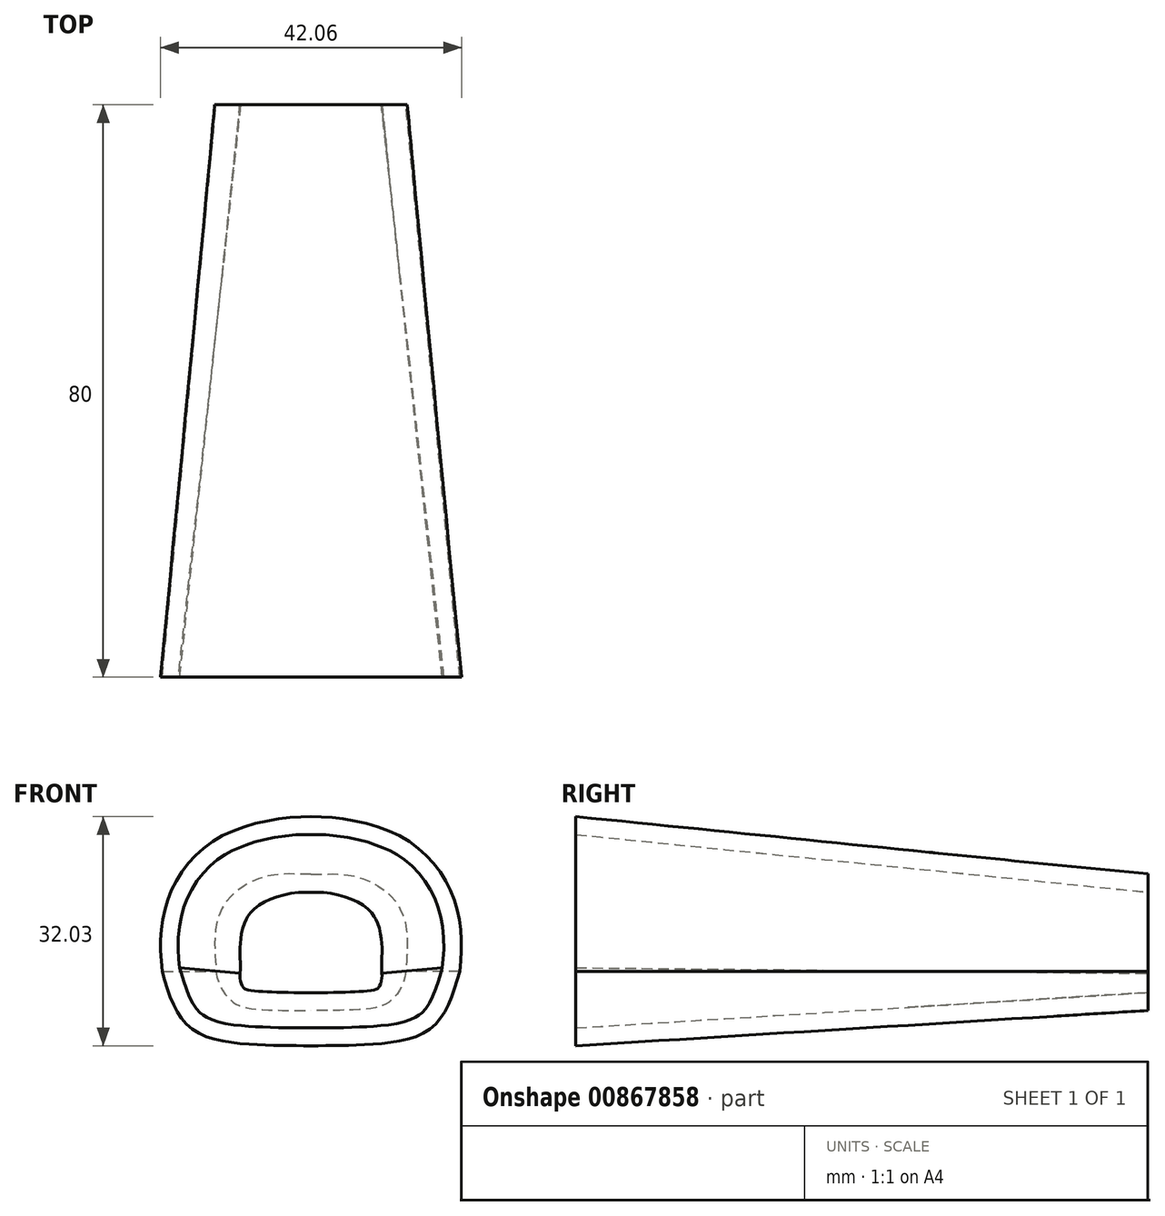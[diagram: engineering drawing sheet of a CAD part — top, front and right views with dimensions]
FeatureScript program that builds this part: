
annotation { "Feature Type Name" : "Feature", "Feature Type Description" : "" }
export const myFeature = defineFeature(function(context is Context, id is Id, definition is map)
    precondition{}
    {
        {
            var Q0;
            Q0=qCreatedBy(makeId("Front.planeOp"),FACE);
            var sketch = newSketch(context, id + "F0", { "sketchPlane" : qUnion([Q0])});
            skCircle(sketch, "E0", {"center": v(0, 50) * mm, "radius": 17.5 * mm, "construction": true});
            skSolve(sketch);
        }
        {
            var Q0;
            Q0=qCreatedBy(makeId("Front.planeOp"),FACE);
            var sketch = newSketch(context, id + "F1", { "sketchPlane" : qUnion([Q0])});
            skPoint(sketch, "E1", {"position": v(0, 50) * mm});
            skFitSpline(sketch, "E2", {"points": [v(-20.8, 50) * mm, v(-19.86, 60.47) * mm, v(-12.52, 68.9) * mm, v(0, 71.66) * mm], "startDerivative": vector(-4.23, 34.04) * mm, "endDerivative": vector(31.33, 0) * mm});
            skLineSegment(sketch, "E3", {"start": v(0, 95) * mm, "end": v(0, 106.5) * mm, "construction": true});
            skFitSpline(sketch, "E4.MirrorCS", {"points": [v(20.8, 50) * mm, v(19.86, 60.47) * mm, v(12.52, 68.9) * mm, v(0, 71.66) * mm], "startDerivative": vector(4.23, 34.04) * mm, "endDerivative": vector(-31.33, 0) * mm});
            skLineSegment(sketch, "E5", {"start": v(-101.18, 50) * mm, "end": v(-77.57, 50) * mm, "construction": true});
            skFitSpline(sketch, "E6", {"points": [v(-20.8, 50) * mm, v(-16.8, 42.08) * mm, v(-7.87, 39.8) * mm, v(0, 39.63) * mm], "startDerivative": vector(8, -27.5) * mm, "endDerivative": vector(23.5, -0.08) * mm});
            skFitSpline(sketch, "E7.MirrorCS", {"points": [v(20.8, 50) * mm, v(16.8, 42.08) * mm, v(7.87, 39.8) * mm, v(0, 39.63) * mm], "startDerivative": vector(-8, -27.5) * mm, "endDerivative": vector(-23.5, -0.08) * mm});
            skFitSpline(sketch, "E8.0", {"points": [v(-18.31, 50.3) * mm, v(-18.48, 51.63) * mm, v(-18.6, 53.56) * mm, v(-18.42, 56) * mm, v(-18.12, 57.75) * mm, v(-17.62, 59.42) * mm, v(-16.9, 61.04) * mm, v(-15.98, 62.58) * mm, v(-14.85, 64) * mm, v(-13.51, 65.28) * mm, v(-12.23, 66.2) * mm, v(-11.11, 66.83) * mm, v(-10.2, 67.26) * mm, v(-9.24, 67.64) * mm, v(-7.9, 68.1) * mm, v(-6.12, 68.55) * mm, v(-3.97, 68.92) * mm, v(-1.88, 69.12) * mm, v(-0.6, 69.16) * mm, v(0, 69.16) * mm], "construction": true});
            skFitSpline(sketch, "E8.1", {"points": [v(-18.4, 50.7) * mm, v(-18.23, 50.13) * mm, v(-17.9, 49) * mm, v(-17.4, 47.47) * mm, v(-16.83, 46.13) * mm, v(-16.21, 45.04) * mm, v(-15.71, 44.45) * mm, v(-15.36, 44.13) * mm, v(-15.12, 43.94) * mm, v(-14.77, 43.7) * mm, v(-14.28, 43.45) * mm, v(-13.52, 43.14) * mm, v(-12.41, 42.82) * mm, v(-10.88, 42.55) * mm, v(-9.52, 42.42) * mm, v(-8.41, 42.34) * mm, v(-7.3, 42.27) * mm, v(-5.96, 42.21) * mm, v(-4.42, 42.17) * mm, v(-2.43, 42.14) * mm, v(-0.97, 42.13) * mm, v(0, 42.13) * mm]});
            skFitSpline(sketch, "E8.2", {"points": [v(18.4, 50.7) * mm, v(18.23, 50.13) * mm, v(17.9, 49) * mm, v(17.4, 47.47) * mm, v(16.83, 46.13) * mm, v(16.21, 45.04) * mm, v(15.71, 44.45) * mm, v(15.36, 44.13) * mm, v(15.12, 43.94) * mm, v(14.77, 43.7) * mm, v(14.28, 43.45) * mm, v(13.52, 43.14) * mm, v(12.41, 42.82) * mm, v(10.88, 42.55) * mm, v(9.52, 42.42) * mm, v(8.41, 42.34) * mm, v(7.3, 42.27) * mm, v(5.96, 42.21) * mm, v(4.42, 42.17) * mm, v(2.43, 42.14) * mm, v(0.97, 42.13) * mm, v(0, 42.13) * mm]});
            skFitSpline(sketch, "E8.3", {"points": [v(18.31, 50.3) * mm, v(18.48, 51.63) * mm, v(18.6, 53.56) * mm, v(18.42, 56) * mm, v(18.12, 57.75) * mm, v(17.62, 59.42) * mm, v(16.9, 61.04) * mm, v(15.98, 62.58) * mm, v(14.85, 64) * mm, v(13.51, 65.28) * mm, v(12.23, 66.2) * mm, v(11.11, 66.83) * mm, v(10.2, 67.26) * mm, v(9.24, 67.64) * mm, v(7.9, 68.1) * mm, v(6.12, 68.55) * mm, v(3.97, 68.92) * mm, v(1.88, 69.12) * mm, v(0.6, 69.16) * mm, v(0, 69.16) * mm]});
            skSolve(sketch);
        }
        {
            var Q0;
            Q0=makeQuery(id+"F1.imprint","IMPRINT",FACE,{"disambiguationData":[TD([[makeQuery(id+"F1.imprint","IMPRINT",EDGE,{"derivedFrom":sQuery(id+"F1.wireOp",EDGE,"E2")}),-1.0]])]});
            var sketch = newSketch(context, id + "F2", { "sketchPlane" : qUnion([Q0])});
            skFitSpline(sketch, "E9.0", {"points": [v(-18.31, 50.3) * mm, v(-18.48, 51.63) * mm, v(-18.6, 53.56) * mm, v(-18.42, 56) * mm, v(-18.12, 57.75) * mm, v(-17.62, 59.42) * mm, v(-16.9, 61.04) * mm, v(-15.98, 62.58) * mm, v(-14.85, 64) * mm, v(-13.51, 65.28) * mm, v(-12.23, 66.2) * mm, v(-11.11, 66.83) * mm, v(-10.2, 67.26) * mm, v(-9.24, 67.64) * mm, v(-7.9, 68.1) * mm, v(-6.12, 68.55) * mm, v(-3.97, 68.92) * mm, v(-1.88, 69.12) * mm, v(-0.6, 69.16) * mm, v(0, 69.16) * mm]});
            skFitSpline(sketch, "E10.0", {"points": [v(-18.4, 50.7) * mm, v(-18.23, 50.13) * mm, v(-17.9, 49) * mm, v(-17.4, 47.47) * mm, v(-16.83, 46.13) * mm, v(-16.21, 45.04) * mm, v(-15.71, 44.45) * mm, v(-15.36, 44.13) * mm, v(-15.12, 43.94) * mm, v(-14.77, 43.7) * mm, v(-14.28, 43.45) * mm, v(-13.52, 43.14) * mm, v(-12.41, 42.82) * mm, v(-10.88, 42.55) * mm, v(-9.52, 42.42) * mm, v(-8.41, 42.34) * mm, v(-7.3, 42.27) * mm, v(-5.96, 42.21) * mm, v(-4.42, 42.17) * mm, v(-2.43, 42.14) * mm, v(-0.97, 42.13) * mm, v(0, 42.13) * mm]});
            skFitSpline(sketch, "E11.0", {"points": [v(18.4, 50.7) * mm, v(18.23, 50.13) * mm, v(17.9, 49) * mm, v(17.4, 47.47) * mm, v(16.83, 46.13) * mm, v(16.21, 45.04) * mm, v(15.71, 44.45) * mm, v(15.36, 44.13) * mm, v(15.12, 43.94) * mm, v(14.77, 43.7) * mm, v(14.28, 43.45) * mm, v(13.52, 43.14) * mm, v(12.41, 42.82) * mm, v(10.88, 42.55) * mm, v(9.52, 42.42) * mm, v(8.41, 42.34) * mm, v(7.3, 42.27) * mm, v(5.96, 42.21) * mm, v(4.42, 42.17) * mm, v(2.43, 42.14) * mm, v(0.97, 42.13) * mm, v(0, 42.13) * mm]});
            skFitSpline(sketch, "E12.0", {"points": [v(18.31, 50.3) * mm, v(18.48, 51.63) * mm, v(18.6, 53.56) * mm, v(18.42, 56) * mm, v(18.12, 57.75) * mm, v(17.62, 59.42) * mm, v(16.9, 61.04) * mm, v(15.98, 62.58) * mm, v(14.85, 64) * mm, v(13.51, 65.28) * mm, v(12.23, 66.2) * mm, v(11.11, 66.83) * mm, v(10.2, 67.26) * mm, v(9.24, 67.64) * mm, v(7.9, 68.1) * mm, v(6.12, 68.55) * mm, v(3.97, 68.92) * mm, v(1.88, 69.12) * mm, v(0.6, 69.16) * mm, v(0, 69.16) * mm]});
            skSolve(sketch);
        }
        {
            var Q0;
            Q0=qCreatedBy(makeId("Front.planeOp"),FACE);
            cPlane(context, id + "F3", {"entities" : qUnion([Q0]), "cplaneType" : CPlaneType.OFFSET, "offset" : 80 * mm, "oppositeDirection" : true, "width" : 150 * mm, "height" : 150 * mm});
        }
        {
            var Q0;
            Q0=qCreatedBy(id+"F3.planeOp",FACE);
            var sketch = newSketch(context, id + "F4", { "sketchPlane" : qUnion([Q0])});
            skPoint(sketch, "E13", {"position": v(0, 50) * mm});
            skFitSpline(sketch, "E14", {"points": [v(0, 63.6) * mm, v(-6.34, 63.28) * mm, v(-12.25, 59.17) * mm, v(-13.45, 53.53) * mm, v(-13.27, 50) * mm], "startDerivative": vector(-22.98, -0.02) * mm, "endDerivative": vector(0.71, -17.06) * mm});
            skFitSpline(sketch, "E15", {"points": [v(-13.27, 50) * mm, v(-11.2, 45.97) * mm, v(-8.1, 44.81) * mm, v(0, 44.56) * mm], "startDerivative": vector(2.22, -18.64) * mm, "endDerivative": vector(12.99, 0) * mm});
            skLineSegment(sketch, "E16", {"start": v(0, 70.63) * mm, "end": v(0, 75.08) * mm, "construction": true});
            skFitSpline(sketch, "E17.MirrorCS", {"points": [v(0, 63.6) * mm, v(6.34, 63.28) * mm, v(12.25, 59.17) * mm, v(13.45, 53.53) * mm, v(13.27, 50) * mm], "startDerivative": vector(22.98, -0.02) * mm, "endDerivative": vector(-0.71, -17.06) * mm});
            skFitSpline(sketch, "E18.MirrorCS", {"points": [v(13.27, 50) * mm, v(11.2, 45.97) * mm, v(8.1, 44.81) * mm, v(0, 44.56) * mm], "startDerivative": vector(-2.22, -18.64) * mm, "endDerivative": vector(-12.99, 0) * mm});
            skFitSpline(sketch, "E19.0", {"points": [v(10.79, 50.3) * mm, v(10.76, 50.03) * mm, v(10.66, 49.56) * mm, v(10.45, 49) * mm, v(10.19, 48.54) * mm, v(9.94, 48.23) * mm, v(9.74, 48.02) * mm, v(9.61, 47.9) * mm, v(9.51, 47.82) * mm, v(9.42, 47.75) * mm, v(9.32, 47.68) * mm, v(9.21, 47.62) * mm, v(9.04, 47.54) * mm, v(8.74, 47.44) * mm, v(8.2, 47.34) * mm, v(7.63, 47.27) * mm, v(6.95, 47.2) * mm, v(5.97, 47.14) * mm, v(4.67, 47.1) * mm, v(3.34, 47.07) * mm, v(2.06, 47.06) * mm, v(0.91, 47.06) * mm, v(0.27, 47.06) * mm, v(0, 47.06) * mm]});
            skFitSpline(sketch, "E19.1", {"points": [v(0, 61.1) * mm, v(0.53, 61.1) * mm, v(1.54, 61.12) * mm, v(2.95, 61.16) * mm, v(4.03, 61.13) * mm, v(4.84, 61.04) * mm, v(5.43, 60.93) * mm, v(6, 60.78) * mm, v(6.6, 60.58) * mm, v(7.18, 60.33) * mm, v(7.95, 59.93) * mm, v(8.66, 59.45) * mm, v(9.26, 58.92) * mm, v(9.66, 58.51) * mm, v(9.98, 58.1) * mm, v(10.23, 57.7) * mm, v(10.44, 57.25) * mm, v(10.67, 56.6) * mm, v(10.86, 55.7) * mm, v(10.94, 54.72) * mm, v(10.96, 53.94) * mm, v(10.95, 53.17) * mm, v(10.91, 52.29) * mm, v(10.84, 51.24) * mm, v(10.79, 50.5) * mm, v(10.77, 50.1) * mm]});
            skFitSpline(sketch, "E19.2", {"points": [v(0, 61.1) * mm, v(-0.53, 61.1) * mm, v(-1.54, 61.12) * mm, v(-2.95, 61.16) * mm, v(-4.03, 61.13) * mm, v(-4.84, 61.04) * mm, v(-5.43, 60.93) * mm, v(-6, 60.78) * mm, v(-6.6, 60.58) * mm, v(-7.18, 60.33) * mm, v(-7.95, 59.93) * mm, v(-8.66, 59.45) * mm, v(-9.26, 58.92) * mm, v(-9.66, 58.51) * mm, v(-9.98, 58.1) * mm, v(-10.23, 57.7) * mm, v(-10.44, 57.25) * mm, v(-10.67, 56.6) * mm, v(-10.86, 55.7) * mm, v(-10.94, 54.72) * mm, v(-10.96, 53.94) * mm, v(-10.95, 53.17) * mm, v(-10.91, 52.29) * mm, v(-10.84, 51.24) * mm, v(-10.79, 50.5) * mm, v(-10.77, 50.1) * mm], "construction": true});
            skFitSpline(sketch, "E19.3", {"points": [v(-10.79, 50.3) * mm, v(-10.76, 50.03) * mm, v(-10.66, 49.56) * mm, v(-10.45, 49) * mm, v(-10.19, 48.54) * mm, v(-9.94, 48.23) * mm, v(-9.74, 48.02) * mm, v(-9.61, 47.9) * mm, v(-9.51, 47.82) * mm, v(-9.42, 47.75) * mm, v(-9.32, 47.68) * mm, v(-9.21, 47.62) * mm, v(-9.04, 47.54) * mm, v(-8.74, 47.44) * mm, v(-8.2, 47.34) * mm, v(-7.63, 47.27) * mm, v(-6.95, 47.2) * mm, v(-5.97, 47.14) * mm, v(-4.67, 47.1) * mm, v(-3.34, 47.07) * mm, v(-2.06, 47.06) * mm, v(-0.91, 47.06) * mm, v(-0.27, 47.06) * mm, v(0, 47.06) * mm]});
            skSolve(sketch);
        }
        {
            var Q0;
            Q0=makeQuery(id+"F4.imprint","IMPRINT",FACE,{"disambiguationData":[TD([[makeQuery(id+"F4.imprint","IMPRINT",EDGE,{"derivedFrom":sQuery(id+"F4.wireOp",EDGE,"E14")}),1.0]])]});
            var sketch = newSketch(context, id + "F5", { "sketchPlane" : qUnion([Q0])});
            skFitSpline(sketch, "E20.0", {"points": [v(0, 61.1) * mm, v(-0.86, 61.09) * mm, v(-2.1, 61.01) * mm, v(-3.69, 60.73) * mm, v(-4.83, 60.42) * mm, v(-5.95, 60) * mm, v(-6.97, 59.47) * mm, v(-7.85, 58.86) * mm, v(-8.42, 58.29) * mm, v(-8.74, 57.87) * mm, v(-8.9, 57.62) * mm, v(-9.05, 57.34) * mm, v(-9.23, 56.96) * mm, v(-9.48, 56.3) * mm, v(-9.67, 55.54) * mm, v(-9.8, 54.77) * mm, v(-9.87, 54.2) * mm, v(-9.9, 53.63) * mm, v(-9.92, 53.1) * mm, v(-9.91, 52.6) * mm, v(-9.9, 51.91) * mm, v(-9.85, 51.02) * mm, v(-9.86, 50.2) * mm, v(-9.9, 49.75) * mm]});
            skFitSpline(sketch, "E21.0", {"points": [v(0, 61.1) * mm, v(0.86, 61.09) * mm, v(2.1, 61.01) * mm, v(3.69, 60.73) * mm, v(4.83, 60.42) * mm, v(5.95, 60) * mm, v(6.97, 59.47) * mm, v(7.85, 58.86) * mm, v(8.42, 58.29) * mm, v(8.74, 57.87) * mm, v(8.9, 57.62) * mm, v(9.05, 57.34) * mm, v(9.23, 56.96) * mm, v(9.48, 56.3) * mm, v(9.67, 55.54) * mm, v(9.8, 54.77) * mm, v(9.87, 54.2) * mm, v(9.9, 53.63) * mm, v(9.92, 53.1) * mm, v(9.91, 52.6) * mm, v(9.9, 51.91) * mm, v(9.85, 51.02) * mm, v(9.86, 50.2) * mm, v(9.9, 49.75) * mm]});
            skFitSpline(sketch, "E22.0", {"points": [v(9.9, 49.82) * mm, v(9.92, 49.58) * mm, v(9.92, 49.13) * mm, v(9.82, 48.57) * mm, v(9.68, 48.14) * mm, v(9.5, 47.83) * mm, v(9.38, 47.68) * mm, v(9.33, 47.63) * mm, v(9.28, 47.6) * mm, v(9.17, 47.54) * mm, v(8.78, 47.43) * mm, v(8.08, 47.32) * mm, v(7.07, 47.22) * mm, v(5.88, 47.15) * mm, v(4.16, 47.1) * mm, v(1.97, 47.06) * mm, v(0.54, 47.06) * mm, v(0, 47.06) * mm]});
            skFitSpline(sketch, "E23.0", {"points": [v(-9.9, 49.82) * mm, v(-9.92, 49.58) * mm, v(-9.92, 49.13) * mm, v(-9.82, 48.57) * mm, v(-9.68, 48.14) * mm, v(-9.5, 47.83) * mm, v(-9.38, 47.68) * mm, v(-9.33, 47.63) * mm, v(-9.28, 47.6) * mm, v(-9.17, 47.54) * mm, v(-8.78, 47.43) * mm, v(-8.08, 47.32) * mm, v(-7.07, 47.22) * mm, v(-5.88, 47.15) * mm, v(-4.16, 47.1) * mm, v(-1.97, 47.06) * mm, v(-0.54, 47.06) * mm, v(0, 47.06) * mm]});
            skSolve(sketch);
        }
        {
            var Q0;
            Q0=makeQuery(id+"F1.imprint","IMPRINT",FACE,{"disambiguationData":[TD([[makeQuery(id+"F1.imprint","IMPRINT",EDGE,{"derivedFrom":sQuery(id+"F1.wireOp",EDGE,"E2")}),-1.0]])]});
            var Q1;
            Q1=makeQuery(id+"F4.imprint","IMPRINT",FACE,{"disambiguationData":[TD([[makeQuery(id+"F4.imprint","IMPRINT",EDGE,{"derivedFrom":sQuery(id+"F4.wireOp",EDGE,"E14")}),1.0]])]});
            loft(context, id + "F6", {"sheetProfilesArray" : [{ "sheetProfileEntities" : qUnion([Q0]) }, { "sheetProfileEntities" : qUnion([Q1]) }]});
        }
        {
            var Q1;
            Q1=makeQuery(id+"F2.imprint","IMPRINT",FACE,{"disambiguationData":[TD([[makeQuery(id+"F2.imprint","IMPRINT",EDGE,{"derivedFrom":sQuery(id+"F2.wireOp",EDGE,"E9.0")}),-1.0]])]});
            var Q2;
            Q2=makeQuery(id+"F5.imprint","IMPRINT",FACE,{"disambiguationData":[TD([[makeQuery(id+"F5.imprint","IMPRINT",EDGE,{"derivedFrom":sQuery(id+"F5.wireOp",EDGE,"E20.0")}),1.0]])]});
            loft(context, id + "F7", {"operationType" : NewBodyOperationType.REMOVE, "sheetProfilesArray" : [{ "sheetProfileEntities" : qUnion([Q1]) }, { "sheetProfileEntities" : qUnion([Q2]) }]});
        }
    });
